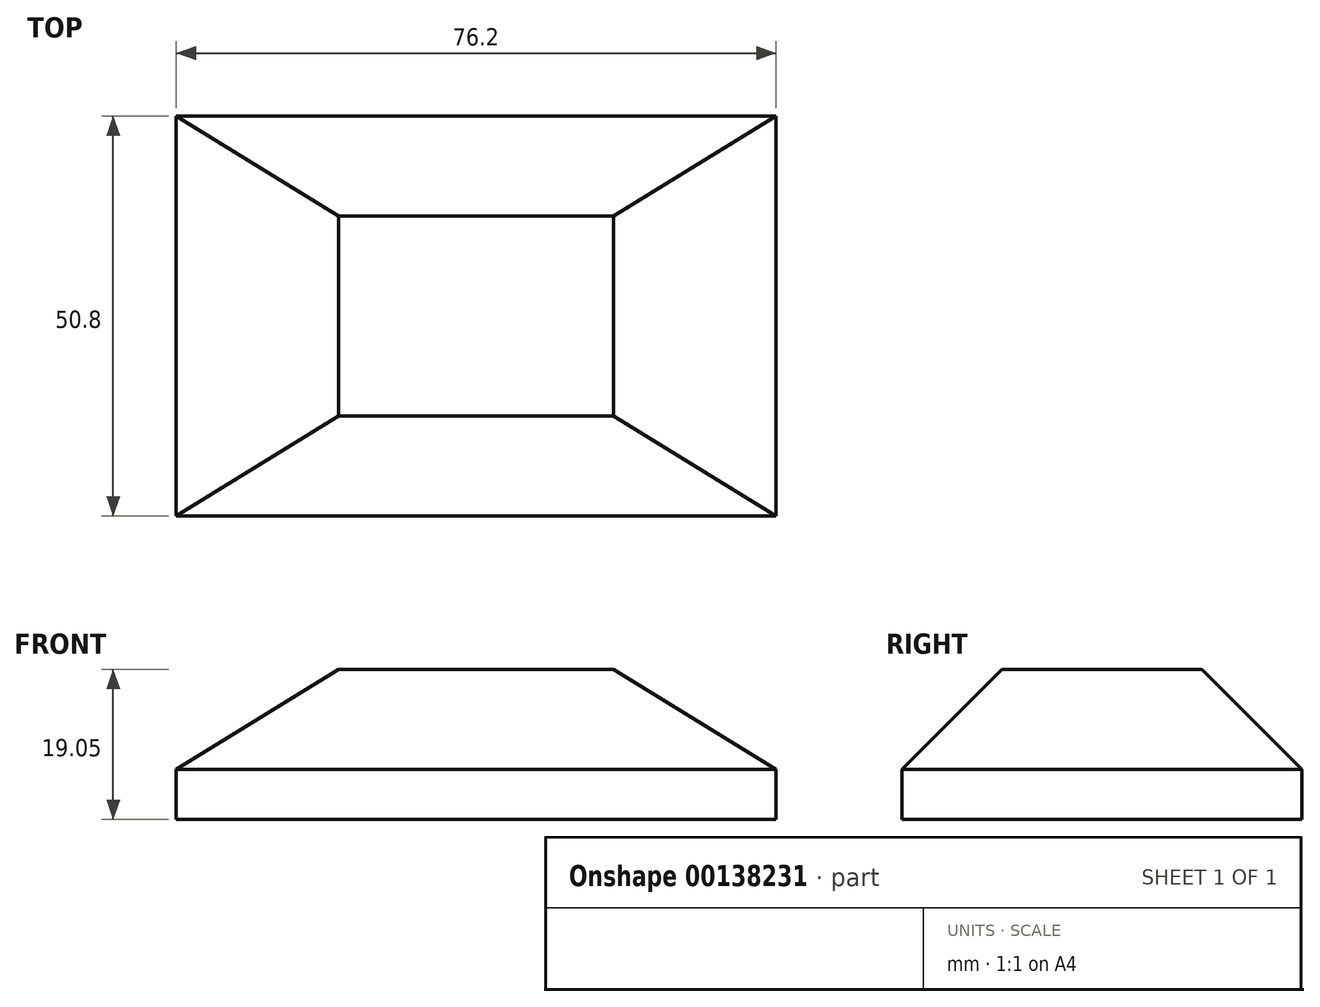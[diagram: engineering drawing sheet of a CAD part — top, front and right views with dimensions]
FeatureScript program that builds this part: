
annotation { "Feature Type Name" : "Feature", "Feature Type Description" : "" }
export const myFeature = defineFeature(function(context is Context, id is Id, definition is map)
    precondition{}
    {
        {
            var Q0;
            Q0=qCreatedBy(makeId("Top.planeOp"),FACE);
            var sketch = newSketch(context, id + "F0", { "sketchPlane" : qUnion([Q0])});
            skLineSegment(sketch, "E0.bottom", {"start": v(0, 0) * mm, "end": v(76.2, 0) * mm});
            skLineSegment(sketch, "E0.top", {"start": v(0, 50.8) * mm, "end": v(76.2, 50.8) * mm});
            skLineSegment(sketch, "E0.left", {"start": v(0, 0) * mm, "end": v(0, 50.8) * mm});
            skLineSegment(sketch, "E0.right", {"start": v(76.2, 0) * mm, "end": v(76.2, 50.8) * mm});
            skSolve(sketch);
        }
        {
            var Q0;
            Q0=makeQuery(id+"F0.imprint","IMPRINT",FACE,{"disambiguationData":[TD([[makeQuery(id+"F0.imprint","IMPRINT",EDGE,{"derivedFrom":sQuery(id+"F0.wireOp",EDGE,"E0.bottom")}),1.0]])]});
            extrude(context, id + "F1", {"entities" : qUnion([Q0]), "oppositeDirection" : true, "depth" : 6.35 * mm});
        }
        {
            var Q0;
            Q0=qCreatedBy(makeId("Top.planeOp"),FACE);
            cPlane(context, id + "F2", {"entities" : qUnion([Q0]), "cplaneType" : CPlaneType.OFFSET, "offset" : 12.7 * mm, "width" : 152.4 * mm, "height" : 152.4 * mm});
        }
        {
            var Q0;
            Q0=qCreatedBy(id+"F2.planeOp",FACE);
            var sketch = newSketch(context, id + "F3", { "sketchPlane" : qUnion([Q0])});
            skLineSegment(sketch, "E1", {"start": v(38.1, 50.8) * mm, "end": v(38.1, 0) * mm, "construction": true});
            skLineSegment(sketch, "E2", {"start": v(0, 25.4) * mm, "end": v(76.2, 25.4) * mm, "construction": true});
            skLineSegment(sketch, "E3.bottom", {"start": v(20.64, 38.1) * mm, "end": v(55.56, 38.1) * mm});
            skLineSegment(sketch, "E3.top", {"start": v(20.64, 12.7) * mm, "end": v(55.56, 12.7) * mm});
            skLineSegment(sketch, "E3.left", {"start": v(20.64, 38.1) * mm, "end": v(20.64, 12.7) * mm});
            skLineSegment(sketch, "E3.right", {"start": v(55.56, 38.1) * mm, "end": v(55.56, 12.7) * mm});
            skSolve(sketch);
        }
        {
            var Q1;
            Q1=makeQuery(id+"F1.opExtrude","CAP_FACE",FACE,{"disambiguationData":[OSD([sQuery(id+"F0.wireOp",EDGE,"E0.bottom"),sQuery(id+"F0.wireOp",EDGE,"E0.top"),sQuery(id+"F0.wireOp",EDGE,"E0.left"),sQuery(id+"F0.wireOp",EDGE,"E0.right")])],"isStart":true});
            var Q2;
            Q2=makeQuery(id+"F3.imprint","IMPRINT",FACE,{"disambiguationData":[TD([[makeQuery(id+"F3.imprint","IMPRINT",EDGE,{"derivedFrom":sQuery(id+"F3.wireOp",EDGE,"E3.bottom")}),-1.0]])]});
            loft(context, id + "F4", {"operationType" : NewBodyOperationType.ADD, "sheetProfilesArray" : [{ "sheetProfileEntities" : qUnion([Q1]) }, { "sheetProfileEntities" : qUnion([Q2]) }]});
        }
    });
